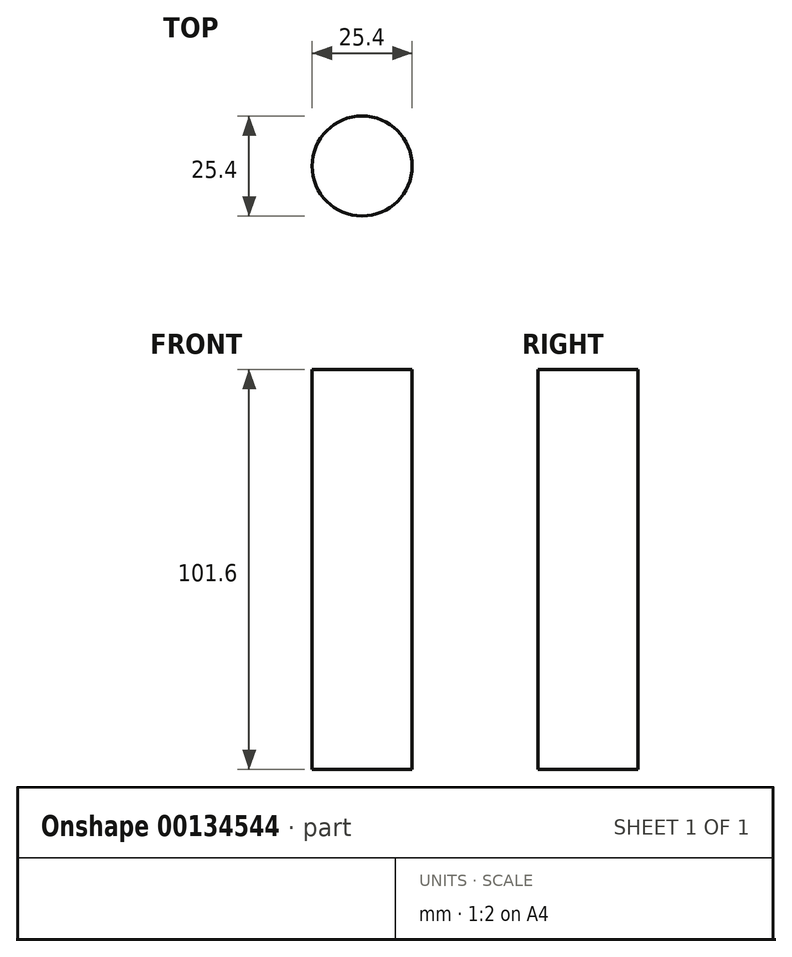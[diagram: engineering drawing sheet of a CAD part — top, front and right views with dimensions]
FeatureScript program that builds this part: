
annotation { "Feature Type Name" : "Feature", "Feature Type Description" : "" }
export const myFeature = defineFeature(function(context is Context, id is Id, definition is map)
    precondition{}
    {
        {
            var Q0;
            Q0=qCreatedBy(makeId("Top.planeOp"),FACE);
            var sketch = newSketch(context, id + "F0", { "sketchPlane" : qUnion([Q0])});
            skCircle(sketch, "E0", {"center": v(0, 0) * mm, "radius": 12.7 * mm});
            skSolve(sketch);
        }
        {
            var Q0;
            Q0 = qSketchRegion(id + "F0", true);
            extrude(context, id + "F1", {"entities" : qUnion([Q0]), "depth" : 101.6 * mm});
        }
    });
